# Revit family: ASH_ArmitageShanks_WallHungHandRinseBasins_Sandringham21-35cm
name_source: partatom
category: Plumbing Fixtures
revit_build: Autodesk Revit MEP 2012 (Build: 20110309_2315(x64)
units: mm (PartAtom-declared; Revit-internal decimal feet)

## types (4) — shared parameters
Accessories = www.idealspec.co.uk
AreaUnits = millimeters
Assembly Code = C1030200
AssetType = Fixed
BasinMaterial = ASH_ArmitageShanks _Sanitaryware_White5_Render
Brand = Armitage Shanks
Category = SanitaryTerminal_WASHHANDBASIN_UK
Color = White
ConnectionType = Plumbing
Default Elevation = 800 mm  [stored 2.62467 ft]
DrainSize = 32 mm  [stored 0.104987 ft]
DurationUnit = year
ECA = No
ExpectedLife = 30
Finish = White
IfcExportAs = IfcSanitaryTerminalType
IfcExportType = WASHHANDBASIN
InstallationInstructions = www.idealspec.co.uk/resources.html
LinearUnits = millimeters
ManufacturerURL = www.idealspec.co.uk
Material = Vitreous china
NBSDescription = Wall hung hand rinse basins
NBSReference = 35-70-70/368
NettWeight = 6.5 Kg
NominalDepth = 260 mm
NominalHeight = 160 mm  [stored 0.524934 ft]
NominalLength = 260 mm
NominalWidth = 351 mm
ProductInformation = www.idealspec.co.uk/assets/datasheet/E892901
Shape = Sculptured
Size = 350 x 260 x 160 mm
Space = Internal
SpareParts = www.fastpart-spares.co.uk
URL = www.idealspec.co.uk
Uniclass2 = Pr_40_20_96_95
Version = 1
VolumeUnits = Litres
WRAS = No
WarrantyDescription = Manufacturers warranty
WarrantyDurationParts = 99
WarrantyDurationUnit = year
WashHandBasinMounting = Wall hung
WashHandBasinType = HANDRINSE
WaterEfficientProduct = No
zero-valued in all types: CWFU, HWFU, WFU

## per-type parameters (varying)
| type | BIMObjectName | Description | E892801 | E892901 | E893001 | Features | Model | ModelNumber | ModelReference | Name | S815001 |
| E892901-Sandringham 21 handrinse washbasin 35cm, left hand taphole, with overflow no chainstay hole | ASH_ArmitageShanks_WallHungHandRinseBasins_Sandringham21_E8929 | Sandringham 21 handrinse washbasin 35 cm, left hand taphole, with overflow no chainstay hole | No | Yes | No | Handrinse washbasin, 35 cm lh taphole | E892901 | E892901 | Sandringham 21 handrinse washbasin 35 cm, left hand taphole, with overflow no chainstay hole | WallHungHandRinseBasins_Sandringham21_E8929_ArmitageShanks | No |
| E892801-Sandringham 21 handrinse washbasin 35cm, right hand taphole, with overflow no chainstay hole | ASH_ArmitageShanks_WallHungHandRinseBasins_Sandringham21_E8928 | Sandringham 21 handrinse washbasin 35 cm, right hand taphole, with overflow no chainstay hole | Yes | No | No | Handrinse washbasin, 35 cm rh taphole | E892801 | E892801 | Sandringham 21 handrinse washbasin 35 cm, right hand taphole, with overflow no chainstay hole | WallHungHandRinseBasins_Sandringham21_E8928_ArmitageShanks | No |
| E893001-Sandringham 21 handrinse washbasin 35cm, 2 taphole, with overflow and chainstay hole | ASH_ArmitageShanks_WallHungHandRinseBasins_Sandringham21_E8930 | Sandringham 21 handrinse washbasin 35 cm, 2 taphole, with overflow and chainstay hole | No | No | Yes | Handrinse washbasin, 35 cm 2 tapholes | E893001 | E893001 | Sandringham 21 handrinse washbasin 35 cm, 2 taphole, with overflow and chainstay hole | WallHungHandRinseBasins_Sandringham21_E8930_ArmitageShanks | No |
| S815001-Sandringham 21 handrinse washbasin 35cm, 2 taphole, no overflow no chainstay hole | ASH_ArmitageShanks_WallHungHandRinseBasins_Sandringham21_S8150 | Sandringham 21 handrinse washbasin 35 cm, 2 taphole, no overflow no chainstay hole | No | No | Yes | Handrinse washbasin, 35 cm 2 tapholes  no overflow or chain | S815001 | S815001 | Sandringham 21 handrinse washbasin 35 cm, 2 taphole, no overflow no chainstay hole | WallHungHandRinseBasins_Sandringham21_S8150_ArmitageShanks | Yes |

note: [stored X ft] marks values corroborated as IEEE doubles in the binary element streams (Revit-internal decimal feet)

## geometry (parser evidence)
native form markers: Blend x1, Sweep x9
no freeform markers — native parametric forms only
